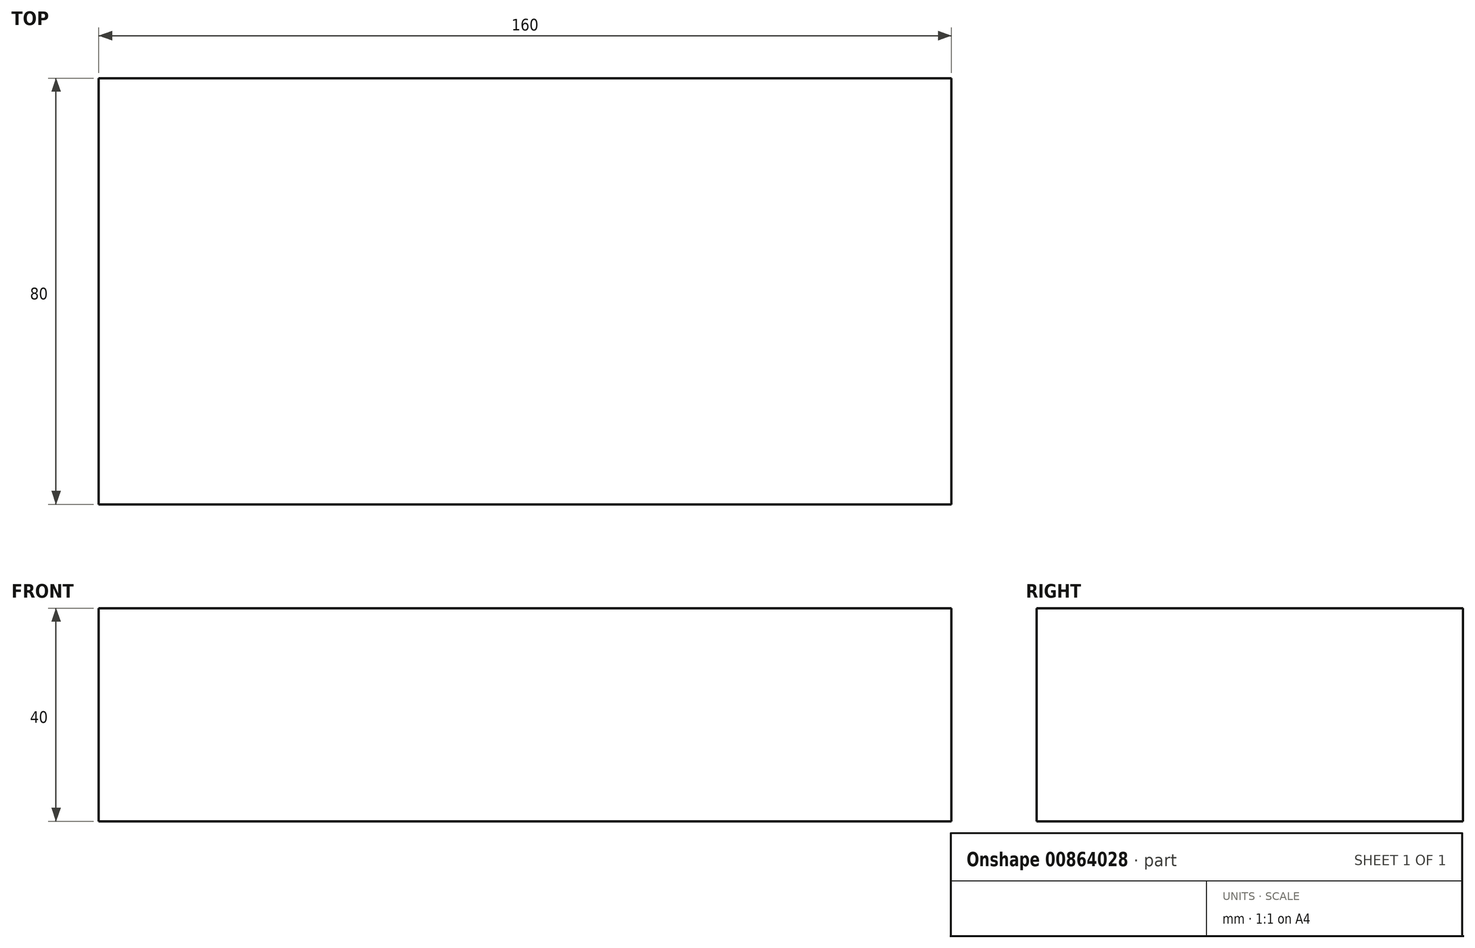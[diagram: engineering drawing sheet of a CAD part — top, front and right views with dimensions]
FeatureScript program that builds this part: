
annotation { "Feature Type Name" : "Feature", "Feature Type Description" : "" }
export const myFeature = defineFeature(function(context is Context, id is Id, definition is map)
    precondition{}
    {
        {
            var Q0;
            Q0=qCreatedBy(makeId("Top.planeOp"),FACE);
            var sketch = newSketch(context, id + "F0", { "sketchPlane" : qUnion([Q0])});
            skLineSegment(sketch, "E0.bottom", {"start": v(-107.04, 71.37) * mm, "end": v(52.96, 71.37) * mm});
            skLineSegment(sketch, "E0.top", {"start": v(-107.04, -8.63) * mm, "end": v(52.96, -8.63) * mm});
            skLineSegment(sketch, "E0.left", {"start": v(-107.04, 71.37) * mm, "end": v(-107.04, -8.63) * mm});
            skLineSegment(sketch, "E0.right", {"start": v(52.96, 71.37) * mm, "end": v(52.96, -8.63) * mm});
            skSolve(sketch);
        }
        {
            var Q0;
            Q0=makeQuery(id+"F0.imprint","IMPRINT",FACE,{"disambiguationData":[TD([[makeQuery(id+"F0.imprint","IMPRINT",EDGE,{"derivedFrom":sQuery(id+"F0.wireOp",EDGE,"E0.bottom")}),-1.0]])]});
            extrude(context, id + "F1", {"entities" : qUnion([Q0]), "depth" : 25.4 * mm, "offsetDistance" : 25.4 * mm});
        }
        {
            var Q0;
            Q0=makeQuery(id+"F0.imprint","IMPRINT",FACE,{"disambiguationData":[TD([[makeQuery(id+"F0.imprint","IMPRINT",EDGE,{"derivedFrom":sQuery(id+"F0.wireOp",EDGE,"E0.bottom")}),-1.0]])]});
            extrude(context, id + "F2", {"entities" : qUnion([Q0]), "operationType" : NewBodyOperationType.ADD, "depth" : 40 * mm, "offsetDistance" : 25 * mm});
        }
        {
            var Q0;
            Q0=makeQuery(id+"F1.opExtrude","CAP_FACE",FACE,{"disambiguationData":[OSD([sQuery(id+"F0.wireOp",EDGE,"E0.bottom"),sQuery(id+"F0.wireOp",EDGE,"E0.top"),sQuery(id+"F0.wireOp",EDGE,"E0.left"),sQuery(id+"F0.wireOp",EDGE,"E0.right")])],"isStart":true});
            var sketch = newSketch(context, id + "F3", { "sketchPlane" : qUnion([Q0])});
            skSolve(sketch);
        }
    });
